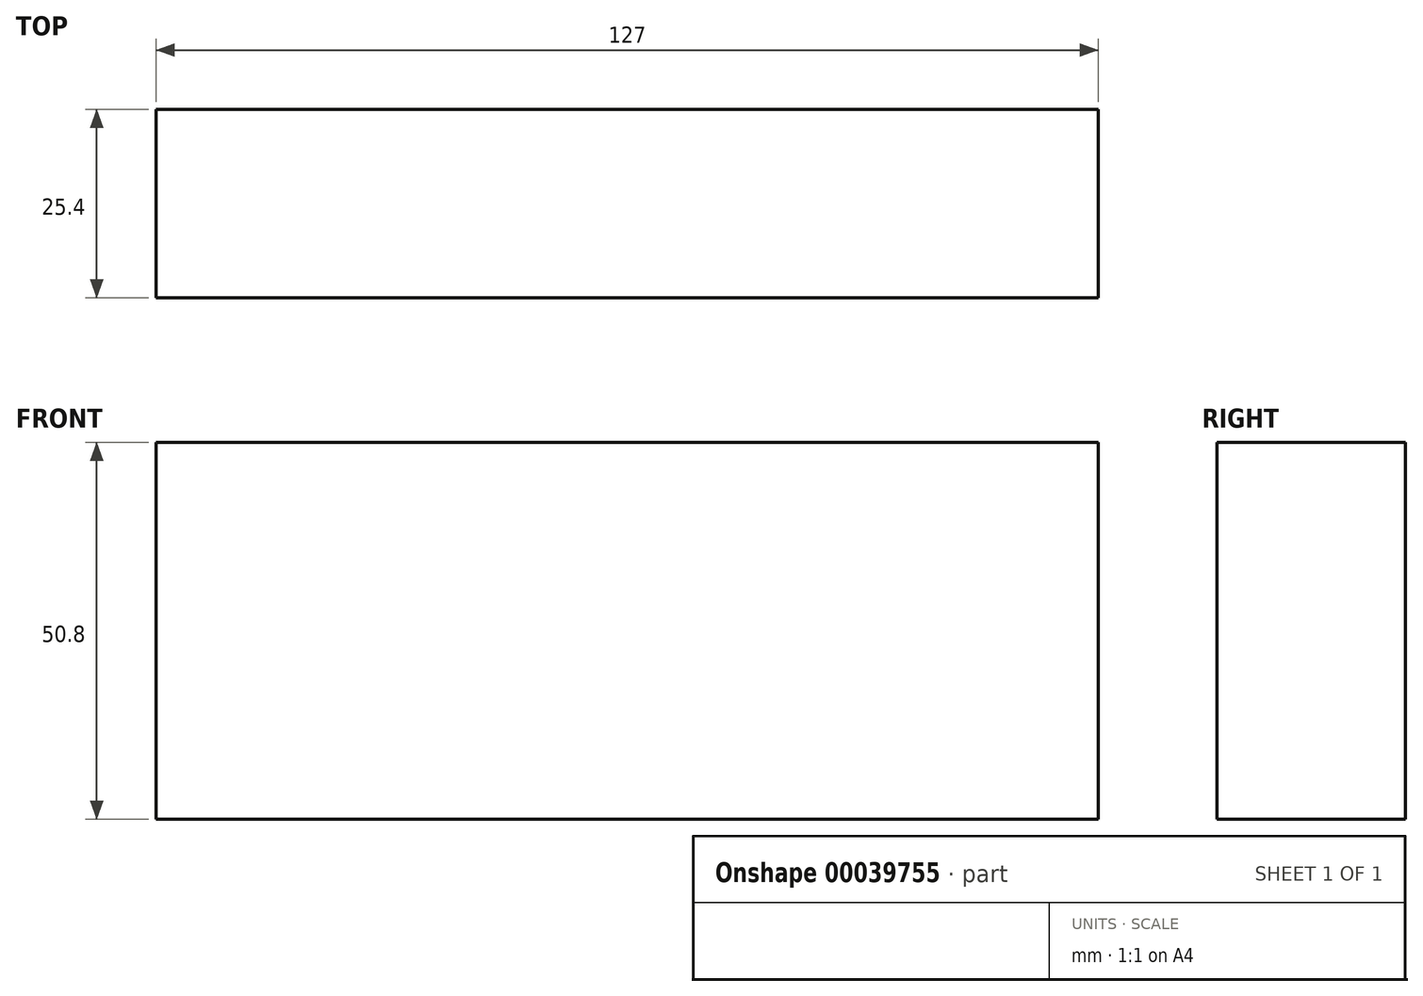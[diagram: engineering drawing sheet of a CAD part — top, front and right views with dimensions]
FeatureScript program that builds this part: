
annotation { "Feature Type Name" : "Feature", "Feature Type Description" : "" }
export const myFeature = defineFeature(function(context is Context, id is Id, definition is map)
    precondition{}
    {
        {
            var Q0;
            Q0=qCreatedBy(makeId("Front.planeOp"),FACE);
            var sketch = newSketch(context, id + "F0", { "sketchPlane" : qUnion([Q0])});
            skLineSegment(sketch, "E0.bottom", {"start": v(0, 0) * mm, "end": v(-127, 0) * mm});
            skLineSegment(sketch, "E0.top", {"start": v(0, 50.8) * mm, "end": v(-127, 50.8) * mm});
            skLineSegment(sketch, "E0.left", {"start": v(0, 0) * mm, "end": v(0, 50.8) * mm});
            skLineSegment(sketch, "E0.right", {"start": v(-127, 0) * mm, "end": v(-127, 50.8) * mm});
            skSolve(sketch);
        }
        {
            var Q0;
            Q0 = qSketchRegion(id + "F0", true);
            extrude(context, id + "F1", {"entities" : qUnion([Q0]), "depth" : 25.4 * mm});
        }
    });
